# Revit family: Faucet-Lavatory-KOHLER-COMPONENTS-K-77958T
name_source: partatom
category: Plumbing Fixtures
revit_build: Autodesk Revit 2017 (Build: 20160225_1515(x64)
units: mm (PartAtom-declared; Revit-internal decimal feet)

## family parameters
Cut with Voids When Loaded = No
Host = Face
OmniClass Number = 23.31.11.00
OmniClass Title = Faucets
Part Type = Normal
Room Calculation Point = No
Round Connector Dimension = Use Diameter
Shared = No

## types (13) — shared parameters
ADA Compliant = No
Assembly Code = D2010
CW Connection = Yes
Cold Water Inlet = Cold Water Inlet
Date Modified = 05/28/2020
Default Elevation = 36"
Flow Rate = 0 GPM
HW Connection = Yes
Handle Clearance = 3 9/16"
Height = 7"
Hot Water Inlet = Hot Water Inlet
Length = 5 1/16"
Manufacturer = KOHLER Co.
MasterFormat 1995 = 15410
MasterFormat 2004 = 22.41.39
Material = Premium Metal Construction
Pressure = 0.00 psi
Product Name = Components
Spout Reach = 5 1/16"
URL = http://www.kohler.com.cn
Vent Connection = No
Waste Connection = No
Waste Water Outlet = Waste Water Outlet
WaterSense Certified = No
Width = 1 7/8"

## per-type parameters (varying)
| type | CW Indexing | Description | Drain Included | Finish | HW Indexing | Handle Lever Finish | Hose | MU Finish | Model | Product Documentation Link | Product Page URL | Type |
| With Lift Rod,CP-Polished Chrome | Kohler-Plastic-Blue | Single-Handle Basin Faucet | Yes | Kohler-Metal-CP-Polished_Chrome | Kohler-Plastic-Red | Kohler-Metal-CP-Polished_Chrome | Yes | Kohler-Metal-CP-Polished_Chrome | K-77958T-4A-CP | http://files.kohler.com.cn | http://www.kohler.com.cn | 1 |
| With Lift Rod,2BL-Original Black | Kohler-Plastic-Blue | Single-Handle Basin Faucet | Yes | Kohler-Metal-2BL-Original_Black | Kohler-Plastic-Red | Kohler-Metal-2BL-Original_Black | Yes | Kohler-Metal-2BL-Original_Black | K-77958T-4A-2BL | http://files.kohler.com.cn | http://www.kohler.com.cn | 2 |
| With Lift Rod,BN-Roman silver | Kohler-Plastic-Blue | Single-Handle Basin Faucet | Yes | Kohler-Metal-BN-Roman_Silver | Kohler-Plastic-Red | Kohler-Metal-BN-Roman_Silver | Yes | Kohler-Metal-BN-Roman_Silver | K-77958T-4A-BN | http://files.kohler.com.cn | http://www.kohler.com.cn | 3 |
| With Lift Rod,RGD-Rose Gold | Kohler-Plastic-Blue | Single-Handle Basin Faucet | Yes | Kohler-Metal-RGD-Rose_Gold | Kohler-Plastic-Red | Kohler-Metal-RGD-Rose_Gold | Yes | Kohler-Metal-RGD-Rose_Gold | K-77958T-4A-RGD | http://files.kohler.com.cn | http://www.kohler.com.cn | 4 |
| With Lift Rod,TT-Titanium Silver | Kohler-Plastic-Blue | Single-Handle Basin Faucet | Yes | Kohler-Metal-TT-Titanium_Silver | Kohler-Plastic-Red | Kohler-Metal-TT-Titanium_Silver | Yes | Kohler-Metal-TT-Titanium_Silver | K-77958T-4A-TT | http://files.kohler.com.cn | http://www.kohler.com.cn | 5 |
| With Lift Rod,3GC-Black Gold | Kohler-Metal-3GC-Black_Gold | Single-Handle Basin Faucet | Yes | Kohler-Metal-3GC-Black_Gold | Kohler-Metal-3GC-Black_Gold | Kohler-Metal-3GC-Black_Gold | Yes | Kohler-Metal-3GC-Black_Gold | K-77958T-4A-3GC | http://files.kohler.com.cn | http://www.kohler.com.cn | 6 |
| With Lift Rod,AF-Flange Gold | Kohler-Plastic-Blue | Single-Handle Basin Faucet | Yes | Kohler-Metal-AF-Flange_Gold | Kohler-Plastic-Red | Kohler-Metal-AF-Flange_Gold | Yes | Kohler-Metal-AF-Flange_Gold | K-77958T-4A-AF | http://files.kohler.com.cn | http://www.kohler.com.cn | 7 |
| Without Lift Rod,CP-Polished Chrome | Kohler-Plastic-Blue | Single-Handle Basin Faucet Without Drain | No | Kohler-Metal-CP-Polished_Chrome | Kohler-Plastic-Red | Kohler-Metal-CP-Polished_Chrome | No | Kohler-Metal-CP-Polished_Chrome | K-77958T-4AND-CP |  |  | 8 |
| Without Lift Rod,BN-Roman Silver | Kohler-Plastic-Blue | Single-Handle Basin Faucet Without Drain | No | Kohler-Metal-BN-Roman_Silver | Kohler-Plastic-Red | Kohler-Metal-BN-Roman_Silver | No | Kohler-Metal-BN-Roman_Silver | K-77958T-4AND-BN |  |  | 9 |
| Without Lift Rod,AF-Flange Gold | Kohler-Plastic-Blue | Single-Handle Basin Faucet Without Drain | No | Kohler-Metal-AF-Flange_Gold | Kohler-Plastic-Red | Kohler-Metal-AF-Flange_Gold | No | Kohler-Metal-AF-Flange_Gold | K-77958T-4AND-AF |  |  | 11 |
| Without Lift Rod,RGD-Rose Gold | Kohler-Plastic-Blue | Single-Handle Basin Faucet Without Drain | No | Kohler-Metal-RGD-Rose_Gold | Kohler-Plastic-Red | Kohler-Metal-RGD-Rose_Gold | No | Kohler-Metal-RGD-Rose_Gold | K-77958T-4AND-RGD |  |  | 10 |
| 4AMU, BLR-Primary Black Red | Kohler-Metal-BL-Matte_Black | Single-handle basin mixer (Manchester United limited edition) | Yes | Kohler-Metal-BL-Matte_Black | Kohler-Metal-BL-Matte_Black | Kohler-Metal-Red | No | Kohler-Metal-Red | K-77958T-4AMU-BLR | https://files.kohler.com.cn | https://www.kohler.com.cn | 12 |
| 4AMU, BL-Primary Black | Kohler-Metal-BL-Matte_Black | Single-handle basin mixer (Manchester United limited edition) | Yes | Kohler-Metal-BL-Matte_Black | Kohler-Metal-BL-Matte_Black | Kohler-Metal-BL-Matte_Black | No | Kohler-Metal-Red | K-77958T-4AMU-BL | https://files.kohler.com.cn | https://www.kohler.com.cn | 13 |

## geometry (parser evidence)
native form markers: Sweep x6
no freeform markers — native parametric forms only
